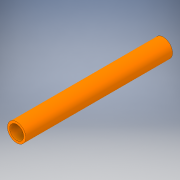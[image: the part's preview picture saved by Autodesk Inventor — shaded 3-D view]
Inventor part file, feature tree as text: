
AUTODESK INVENTOR PART (.ipt)
format: ipt  version: 2018.2 (Build 222227000, 227)  size: 107,008 bytes
history: native  units: in
note: dims shown in document units (in); Inventor stores cm internally (conversion verified against a paired STEP export)
features: extrude x1, sketch x1
ambient origin geometry x8: Origin, YZ Plane, XZ Plane, XY Plane, X Axis, Y Axis, Z Axis, Center Point
bodies: Solid1 (feature_tree)
feature tree (2):
  extrude  "Extrusion1"  Depth=10.5in
  sketch  "Sketch1"  dims[d0=1.315in d1=1.0in d2=10.5in d3=0.0in]
